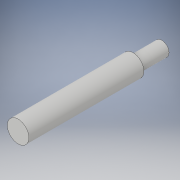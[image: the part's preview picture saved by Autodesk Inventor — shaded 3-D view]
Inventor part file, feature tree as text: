
AUTODESK INVENTOR PART (.ipt)
format: ipt  version: 2019 (Build 230136000, 136)  size: 99,328 bytes
history: native  units: in
note: dims shown in document units (in); Inventor stores cm internally (conversion verified against a paired STEP export)
features: extrude x2, sketch x2
ambient origin geometry x8: Origin, YZ Plane, XZ Plane, XY Plane, X Axis, Y Axis, Z Axis, Center Point
bodies: Solid1 (feature_tree)
feature tree (4):
  extrude  "Extrusion1"  Depth=5.0in TaperAngle=0.0deg
  extrude  "Extrusion2"  Depth=4.0in TaperAngle=0.0deg
  sketch  "Sketch1"  dims[d0=0.5in d1=5.0in d2=0.0in]
  sketch  "Sketch2"  dims[d3=0.75in d4=4.0in d5=0.0in]
